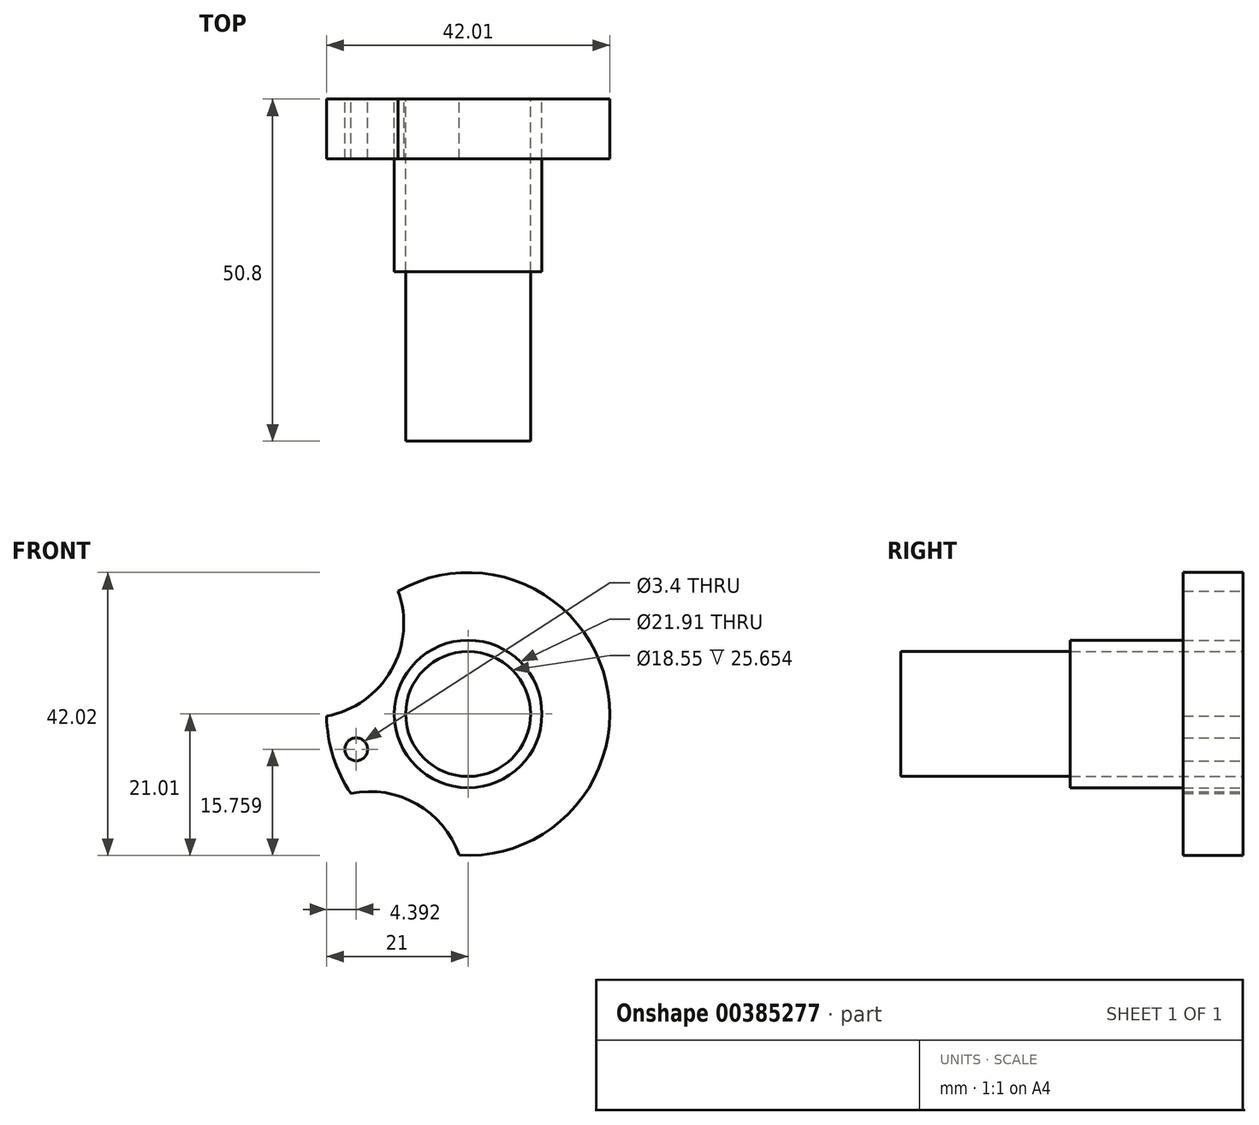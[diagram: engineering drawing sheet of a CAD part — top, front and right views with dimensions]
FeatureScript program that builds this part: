
annotation { "Feature Type Name" : "Feature", "Feature Type Description" : "" }
export const myFeature = defineFeature(function(context is Context, id is Id, definition is map)
    precondition{}
    {
        {
            var Q0;
            Q0=qCreatedBy(makeId("Front.planeOp"),FACE);
            var sketch = newSketch(context, id + "F0", { "sketchPlane" : qUnion([Q0])});
            skArc(sketch, "E0", {"start": v(-1.34, -20.96) * mm, "mid": v(20.47, 4.73) * mm, "end": v(-10.4, 18.25) * mm});
            skArc(sketch, "E1", {"start": v(-1.34, -20.96) * mm, "mid": v(-7.63, -13.35) * mm, "end": v(-17.38, -11.8) * mm});
            skArc(sketch, "E2", {"start": v(-21, -0.31) * mm, "mid": v(-11.39, 6.5) * mm, "end": v(-10.4, 18.25) * mm});
            skArc(sketch, "E3.trimOffspring", {"start": v(-21, -0.31) * mm, "mid": v(-20.03, -6.32) * mm, "end": v(-17.38, -11.8) * mm});
            skCircle(sketch, "E4", {"center": v(-16.6, -5.25) * mm, "radius": 1.7 * mm});
            skCircle(sketch, "E5", {"center": v(0, 0) * mm, "radius": 10.96 * mm});
            skCircle(sketch, "E6", {"center": v(0, 0) * mm, "radius": 9.27 * mm});
            skSolve(sketch);
        }
        {
            var Q0;
            Q0=makeQuery(id+"F0.imprint","IMPRINT",FACE,{"disambiguationData":[TD([[makeQuery(id+"F0.imprint","IMPRINT",EDGE,{"derivedFrom":sQuery(id+"F0.wireOp",EDGE,"E6")}),1.0]])]});
            extrude(context, id + "F1", {"entities" : qUnion([Q0]), "depth" : 50.8 * mm});
        }
        {
            var Q0;
            Q0=makeQuery(id+"F0.imprint","IMPRINT",FACE,{"disambiguationData":[TD([[makeQuery(id+"F0.imprint","IMPRINT",EDGE,{"derivedFrom":sQuery(id+"F0.wireOp",EDGE,"E0")}),1.0]])]});
            extrude(context, id + "F2", {"entities" : qUnion([Q0]), "depth" : 8.9 * mm});
        }
        {
            var Q0;
            Q0=makeQuery(id+"F0.imprint","IMPRINT",FACE,{"disambiguationData":[TD([[makeQuery(id+"F0.imprint","IMPRINT",EDGE,{"derivedFrom":sQuery(id+"F0.wireOp",EDGE,"E5")}),1.0]])]});
            extrude(context, id + "F3", {"entities" : qUnion([Q0]), "depth" : 25.65 * mm});
        }
    });
